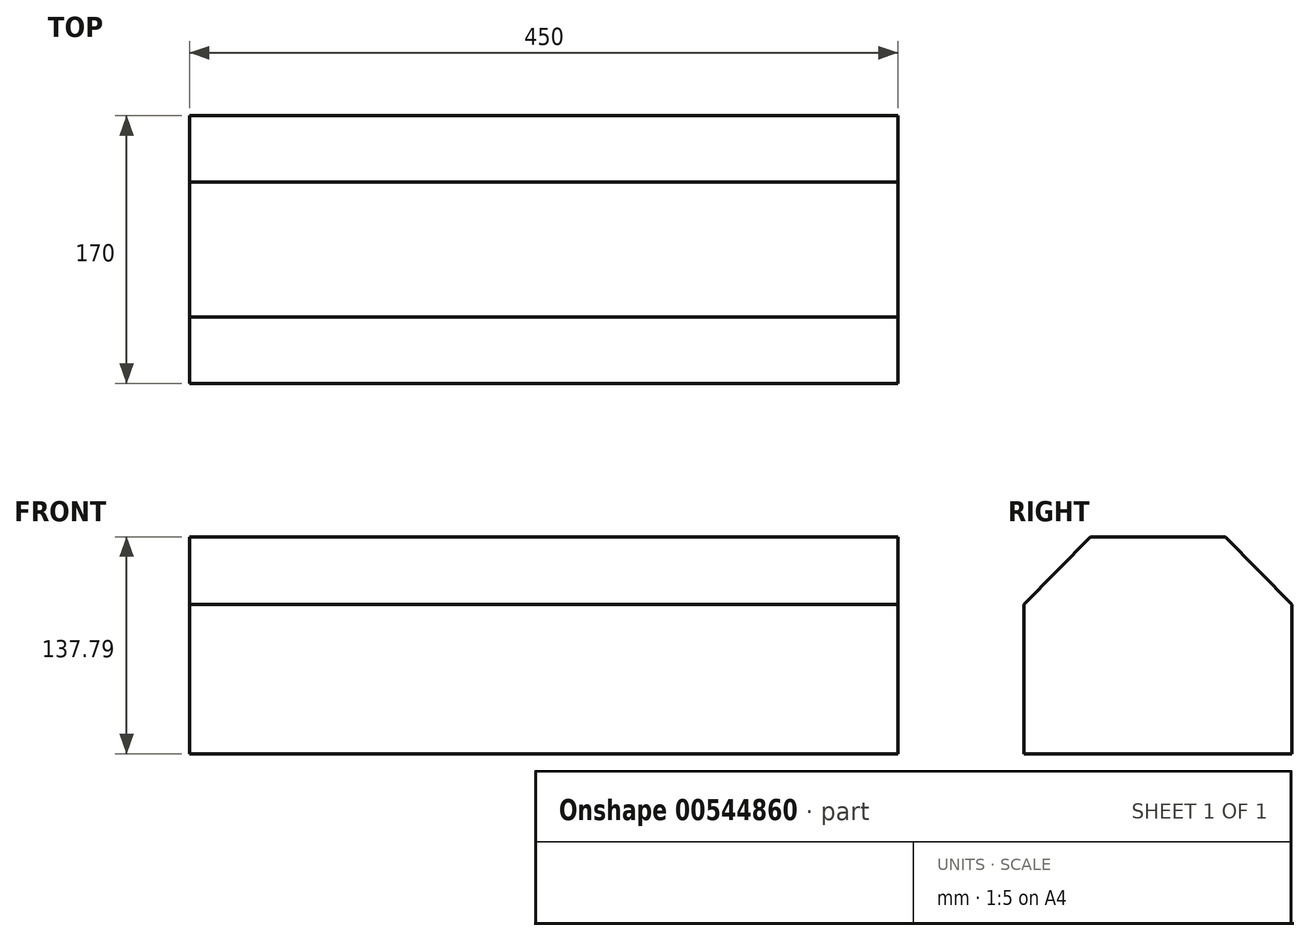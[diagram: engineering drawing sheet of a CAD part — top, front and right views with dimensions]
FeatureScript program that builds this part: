
annotation { "Feature Type Name" : "Feature", "Feature Type Description" : "" }
export const myFeature = defineFeature(function(context is Context, id is Id, definition is map)
    precondition{}
    {
        {
            var Q0;
            Q0=qCreatedBy(makeId("Right.planeOp"),FACE);
            var sketch = newSketch(context, id + "F0", { "sketchPlane" : qUnion([Q0])});
            skLineSegment(sketch, "E0", {"start": v(0, 0) * mm, "end": v(170, 0) * mm});
            skLineSegment(sketch, "E1", {"start": v(170, 0) * mm, "end": v(170, 95) * mm});
            skLineSegment(sketch, "E2", {"start": v(170, 95) * mm, "end": v(127.94, 137.79) * mm});
            skLineSegment(sketch, "E3", {"start": v(127.94, 137.79) * mm, "end": v(42.06, 137.79) * mm});
            skLineSegment(sketch, "E4", {"start": v(42.06, 137.79) * mm, "end": v(0, 95) * mm});
            skLineSegment(sketch, "E5", {"start": v(0, 0) * mm, "end": v(0, 95) * mm});
            skSolve(sketch);
        }
        {
            var Q0;
            Q0=makeQuery(id+"F0.imprint","IMPRINT",FACE,{"disambiguationData":[TD([[makeQuery(id+"F0.imprint","IMPRINT",EDGE,{"derivedFrom":sQuery(id+"F0.wireOp",EDGE,"E0")}),1.0]])]});
            extrude(context, id + "F1", {"entities" : qUnion([Q0]), "depth" : 450 * mm, "offsetDistance" : 25 * mm});
        }
    });
